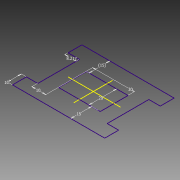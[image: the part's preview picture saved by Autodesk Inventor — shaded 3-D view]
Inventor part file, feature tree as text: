
AUTODESK INVENTOR PART (.ipt)
format: ipt  version: 2015 (Build 190159000, 159)  size: 72,192 bytes
history: native  units: mm
features: sketch x1
ambient origin geometry x8: Origin, YZ Plane, XZ Plane, XY Plane, X Axis, Y Axis, Z Axis, Center Point
feature tree (1):
  sketch  "Sketch1"  dims[d0=10.0mm d2=8.217mm d3=10.0mm d5=20.0mm d6=30.0mm d7=15.0mm d8=15.0mm]
